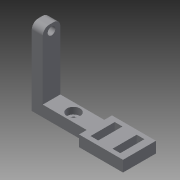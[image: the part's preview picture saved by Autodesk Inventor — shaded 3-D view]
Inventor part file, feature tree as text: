
AUTODESK INVENTOR PART (.ipt)
format: ipt  version: 2013 SP2 (Build 170200200, 200)  size: 124,928 bytes
history: native  units: mm
features: extrude x4, sketch x4, fillet x1
ambient origin geometry x8: Origin, YZ Plane, XZ Plane, XY Plane, X Axis, Y Axis, Z Axis, Center Point
bodies: Solid1 (feature_tree)
feature tree (9):
  extrude  "Extrusion1"  Depth=15.0mm
  extrude  "Extrusion2"  Depth=8.0mm
  extrude  "Extrusion3"  Depth=30.0mm TaperAngle=0.0deg
  fillet  "Fillet1"  Radius=3.5mm
  extrude  "Extrusion4"  Depth=35.0mm TaperAngle=0.0deg
  sketch  "Sketch1"  dims[d0=20.0mm d1=2.0mm d2=2.0mm d3=3.5mm d4=3.25mm d5=6.5mm d6=3.5mm d8=15.0mm]
  sketch  "Sketch2"  dims[d9=25.0mm d10=8.0mm]
  sketch  "Sketch3"  dims[d11=5.0mm d12=0.0mm d15=30.0mm d16=0.0mm d17=3.5mm]
  sketch  "Sketch4"  dims[d18=3.0mm d19=35.0mm d20=0.0mm d21=3.0mm d22=3.5mm d23=10.0mm d24=5.0mm d26=6.0mm d28=3.0mm d29=0.0mm]
